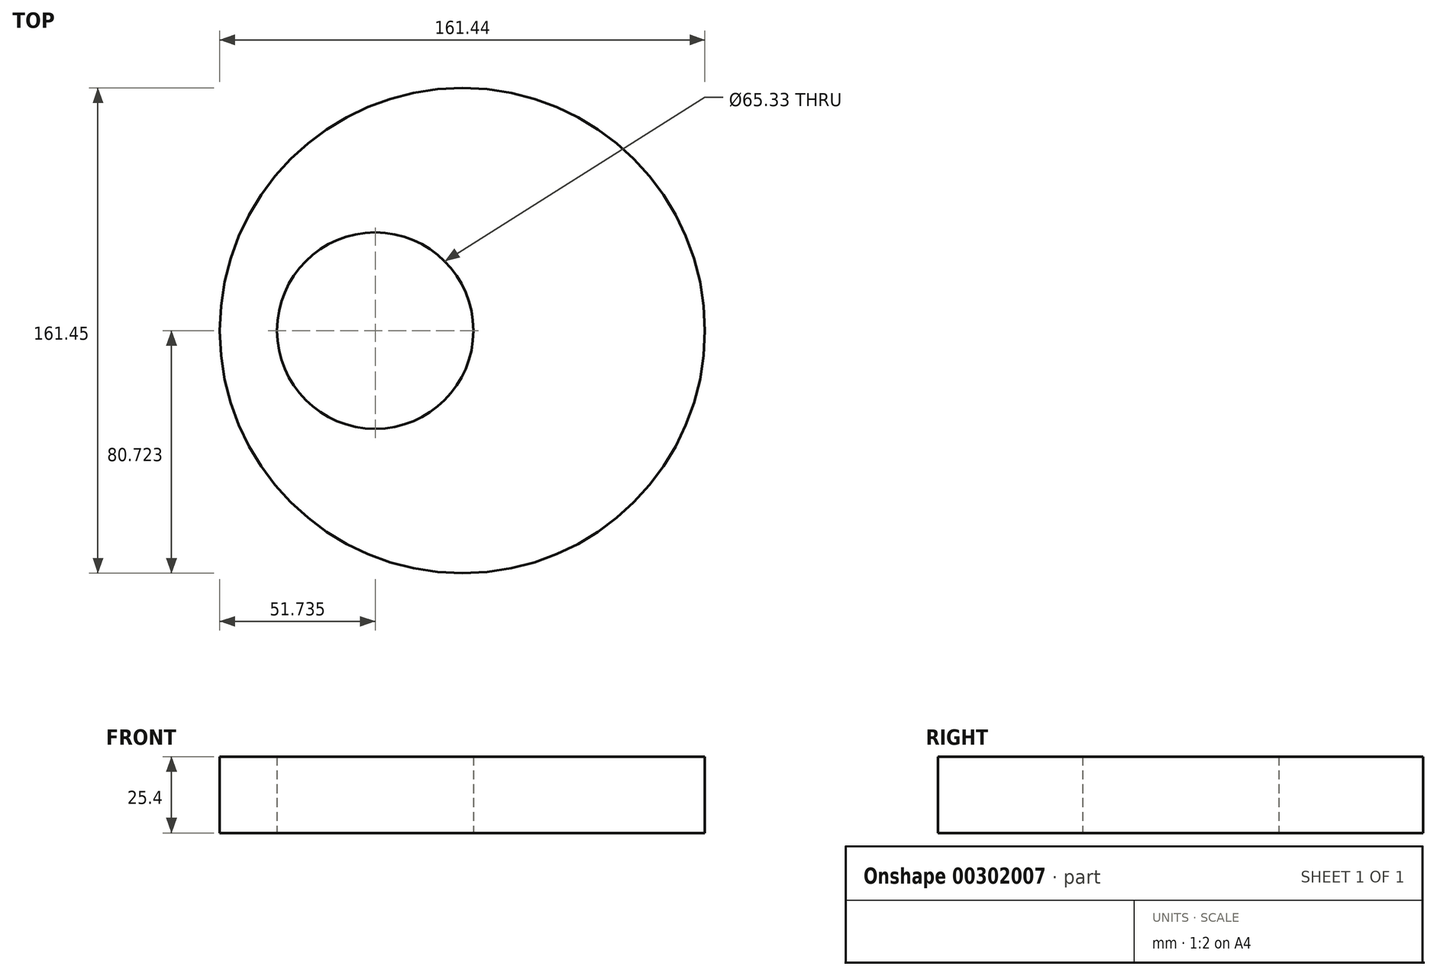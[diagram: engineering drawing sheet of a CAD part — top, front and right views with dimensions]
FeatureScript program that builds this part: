
annotation { "Feature Type Name" : "Feature", "Feature Type Description" : "" }
export const myFeature = defineFeature(function(context is Context, id is Id, definition is map)
    precondition{}
    {
        {
            var Q0;
            Q0=qCreatedBy(makeId("Top.planeOp"),FACE);
            var sketch = newSketch(context, id + "F0", { "sketchPlane" : qUnion([Q0])});
            skCircle(sketch, "E0", {"center": v(-37.3, -35.08) * mm, "radius": 80.72 * mm});
            skCircle(sketch, "E1", {"center": v(-66.29, -35.08) * mm, "radius": 32.66 * mm});
            skSolve(sketch);
        }
        {
            var Q0;
            Q0=makeQuery(id+"F0.imprint","IMPRINT",FACE,{"disambiguationData":[TD([[makeQuery(id+"F0.imprint","IMPRINT",EDGE,{"derivedFrom":sQuery(id+"F0.wireOp",EDGE,"E0")}),1.0]])]});
            extrude(context, id + "F1", {"entities" : qUnion([Q0]), "depth" : 25.4 * mm, "offsetDistance" : 25.4 * mm});
        }
    });
